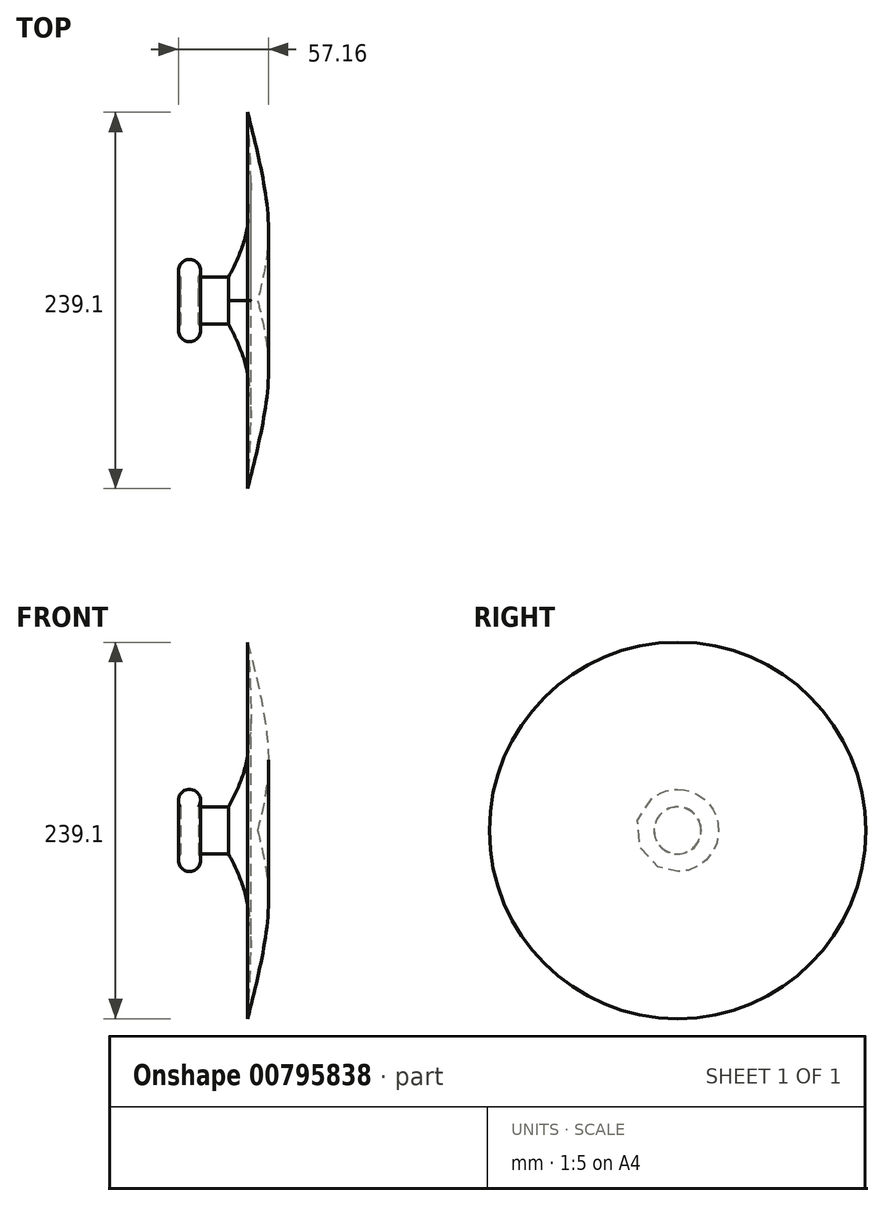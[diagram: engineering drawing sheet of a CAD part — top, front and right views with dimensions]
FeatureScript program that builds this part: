
annotation { "Feature Type Name" : "Feature", "Feature Type Description" : "" }
export const myFeature = defineFeature(function(context is Context, id is Id, definition is map)
    precondition{}
    {
        {
            var Q0;
            Q0=qCreatedBy(makeId("Front.planeOp"),FACE);
            var sketch = newSketch(context, id + "F0", { "sketchPlane" : qUnion([Q0])});
            skFitSpline(sketch, "E0", {"points": [v(31.26, 119.55) * mm, v(44.4, 47.04) * mm, v(37.57, 0) * mm], "startDerivative": vector(34.5, -137.71) * mm, "endDerivative": vector(-24.02, -100.01) * mm});
            skFitSpline(sketch, "E1", {"points": [v(31.26, 119.55) * mm, v(31.26, 47.04) * mm, v(19.18, 15.04) * mm], "startDerivative": vector(8.8, -135.27) * mm, "endDerivative": vector(-35.72, -69.7) * mm});
            skLineSegment(sketch, "E2", {"start": v(19.18, 15.04) * mm, "end": v(0, 15.04) * mm});
            skPoint(sketch, "E3.end.orphan", {"position": v(-11.3, 14.85) * mm});
            skArc(sketch, "E4", {"start": v(0, 15.04) * mm, "mid": v(-5.84, 26.14) * mm, "end": v(-11.3, 14.85) * mm});
            skLineSegment(sketch, "E5", {"start": v(-11.3, 14.85) * mm, "end": v(-11.3, 0) * mm});
            skLineSegment(sketch, "E6", {"start": v(-11.3, 0) * mm, "end": v(37.57, 0) * mm});
            skSolve(sketch);
        }
        {
            var Q0;
            Q0 = qSketchRegion(id + "F0", true);
            var Q1;
            Q1=sQuery(id+"F0.wireOp",EDGE,"E6");
            revolve(context, id + "F1", {"surfaceOperationType" : NewSurfaceOperationType.NEW, "entities" : qUnion([Q0]), "axis" : qUnion([Q1]), "revolveType" : RevolveType.FULL});
        }
    });
